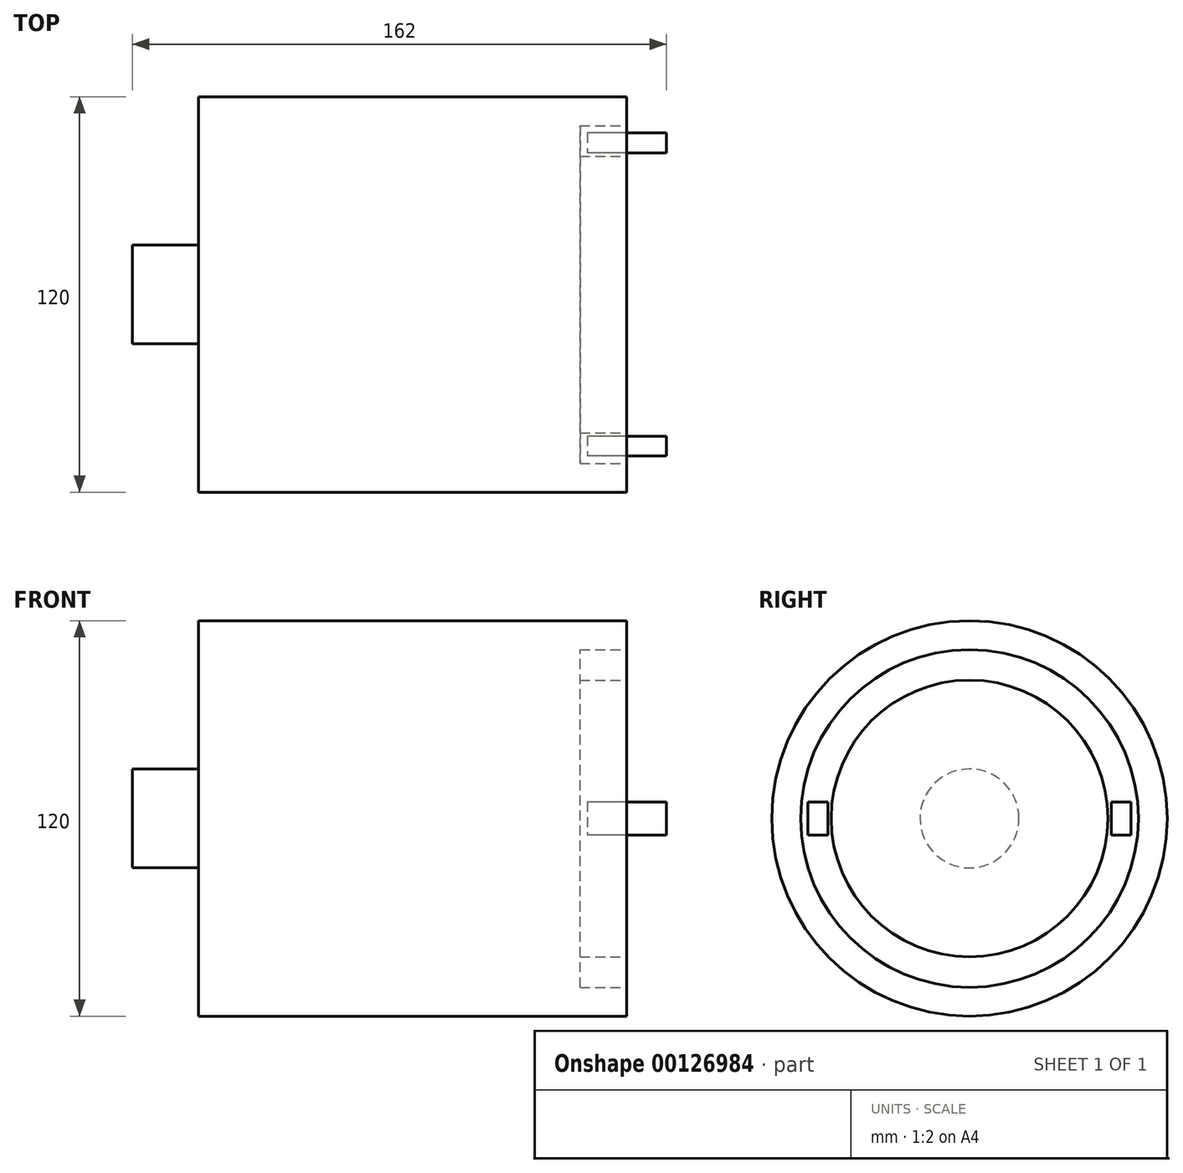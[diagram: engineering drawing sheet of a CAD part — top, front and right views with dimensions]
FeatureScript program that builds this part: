
annotation { "Feature Type Name" : "Feature", "Feature Type Description" : "" }
export const myFeature = defineFeature(function(context is Context, id is Id, definition is map)
    precondition{}
    {
        {
            var Q0;
            Q0=qCreatedBy(makeId("Front.planeOp"),FACE);
            var sketch = newSketch(context, id + "F0", { "sketchPlane" : qUnion([Q0])});
            skLineSegment(sketch, "E0", {"start": v(0, 0) * mm, "end": v(-150, 0) * mm});
            skLineSegment(sketch, "E1", {"start": v(-150, 0) * mm, "end": v(-150, 15) * mm});
            skLineSegment(sketch, "E2", {"start": v(-150, 15) * mm, "end": v(-130, 15) * mm});
            skLineSegment(sketch, "E3", {"start": v(-130, 15) * mm, "end": v(-130, 60) * mm});
            skLineSegment(sketch, "E4", {"start": v(-130, 60) * mm, "end": v(0, 60) * mm});
            skLineSegment(sketch, "E5", {"start": v(0, 60) * mm, "end": v(0, 51.24) * mm});
            skLineSegment(sketch, "E6.bottom", {"start": v(0, 41.97) * mm, "end": v(-14.17, 41.97) * mm});
            skLineSegment(sketch, "E6.top", {"start": v(0, 51.24) * mm, "end": v(-14.17, 51.24) * mm});
            skLineSegment(sketch, "E6.right", {"start": v(-14.17, 41.97) * mm, "end": v(-14.17, 51.24) * mm});
            skLineSegment(sketch, "E7.trimOffspring", {"start": v(0, 41.97) * mm, "end": v(0, 0) * mm});
            skSolve(sketch);
        }
        {
            var Q0;
            Q0=makeQuery(id+"F0.imprint","IMPRINT",FACE,{"disambiguationData":[TD([[makeQuery(id+"F0.imprint","IMPRINT",EDGE,{"derivedFrom":sQuery(id+"F0.wireOp",EDGE,"E0")}),-1.0]])]});
            var Q1;
            Q1=sQuery(id+"F0.wireOp",EDGE,"E0");
            revolve(context, id + "F1", {"entities" : qUnion([Q0]), "axis" : qUnion([Q1]), "revolveType" : RevolveType.FULL});
        }
        {
            var Q0;
            Q0=qCreatedBy(makeId("Right.planeOp"),FACE);
            var sketch = newSketch(context, id + "F2", { "sketchPlane" : qUnion([Q0])});
            skLineSegment(sketch, "E8.bottom", {"start": v(-43, 5) * mm, "end": v(-49, 5) * mm});
            skLineSegment(sketch, "E8.top", {"start": v(-43, -5) * mm, "end": v(-49, -5) * mm});
            skLineSegment(sketch, "E8.left", {"start": v(-43, 5) * mm, "end": v(-43, -5) * mm});
            skLineSegment(sketch, "E8.right", {"start": v(-49, 5) * mm, "end": v(-49, -5) * mm});
            skPoint(sketch, "E8.middle", {"position": v(-46, 0) * mm});
            skLineSegment(sketch, "E9.bottom", {"start": v(49, 5) * mm, "end": v(43, 5) * mm});
            skLineSegment(sketch, "E9.top", {"start": v(49, -5) * mm, "end": v(43, -5) * mm});
            skLineSegment(sketch, "E9.left", {"start": v(49, 5) * mm, "end": v(49, -5) * mm});
            skLineSegment(sketch, "E9.right", {"start": v(43, 5) * mm, "end": v(43, -5) * mm});
            skPoint(sketch, "E9.middle", {"position": v(46, 0) * mm});
            skSolve(sketch);
        }
        {
            var Q0;
            Q0 = qSketchRegion(id + "F2", true);
            extrude(context, id + "F3", {"entities" : qUnion([Q0]), "endBound" : BoundingType.SYMMETRIC, "depth" : 24 * mm});
        }
    });
